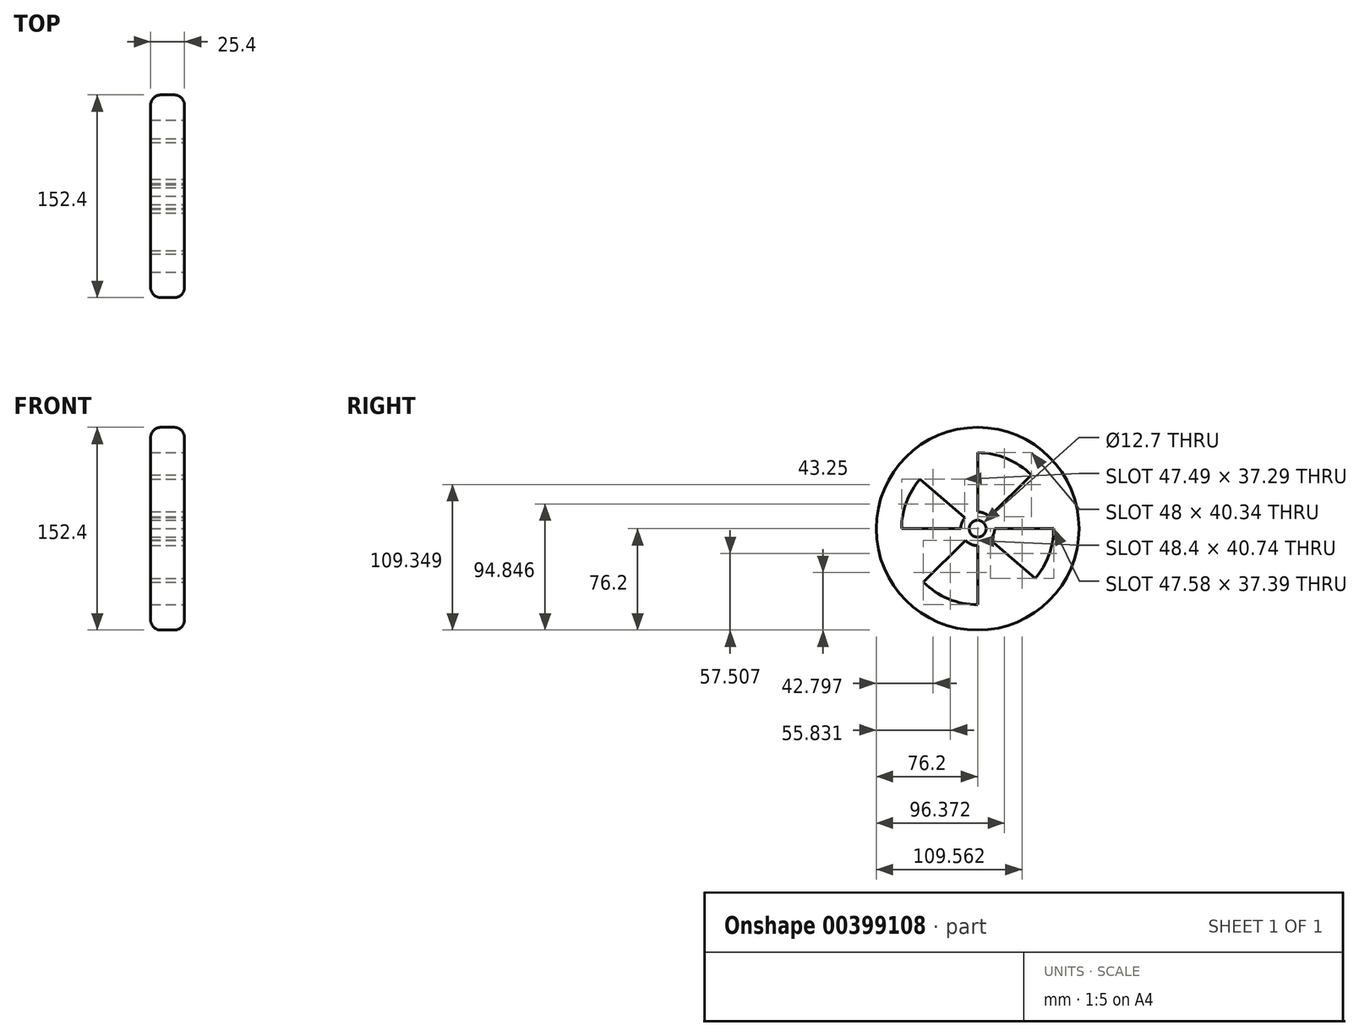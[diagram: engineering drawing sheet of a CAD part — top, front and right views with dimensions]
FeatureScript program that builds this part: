
annotation { "Feature Type Name" : "Feature", "Feature Type Description" : "" }
export const myFeature = defineFeature(function(context is Context, id is Id, definition is map)
    precondition{}
    {
        {
            var Q0;
            Q0=qCreatedBy(makeId("Right.planeOp"),FACE);
            var sketch = newSketch(context, id + "F0", { "sketchPlane" : qUnion([Q0])});
            skCircle(sketch, "E0", {"center": v(0, 0) * mm, "radius": 76.2 * mm});
            skSolve(sketch);
        }
        {
            var Q0;
            Q0=makeQuery(id+"F0.imprint","IMPRINT",FACE,{"disambiguationData":[TD([[makeQuery(id+"F0.imprint","IMPRINT",EDGE,{"derivedFrom":sQuery(id+"F0.wireOp",EDGE,"E0")}),1.0]])]});
            extrude(context, id + "F1", {"entities" : qUnion([Q0]), "depth" : 25.4 * mm});
        }
        {
            var Q0;
            Q0=makeQuery(id+"F1.opExtrude","CAP_FACE",FACE,{"disambiguationData":[OSD([sQuery(id+"F0.wireOp",EDGE,"E0")])],"isStart":false});
            var sketch = newSketch(context, id + "F2", { "sketchPlane" : qUnion([Q0])});
            skCircle(sketch, "E1", {"center": v(0, 0) * mm, "radius": 6.35 * mm});
            skSolve(sketch);
        }
        {
            var Q0;
            Q0=makeQuery(id+"F2.imprint","IMPRINT",FACE,{"disambiguationData":[TD([[makeQuery(id+"F2.imprint","IMPRINT",EDGE,{"derivedFrom":sQuery(id+"F2.wireOp",EDGE,"E1")}),1.0]])]});
            extrude(context, id + "F3", {"entities" : qUnion([Q0]), "operationType" : NewBodyOperationType.REMOVE, "oppositeDirection" : true, "depth" : 25.4 * mm});
        }
        {
            var Q0;
            Q0=makeQuery(id+"F1.opExtrude","CAP_FACE",FACE,{"disambiguationData":[OSD([sQuery(id+"F0.wireOp",EDGE,"E0")])],"isStart":false});
            var sketch = newSketch(context, id + "F4", { "sketchPlane" : qUnion([Q0])});
            skCircle(sketch, "E2", {"center": v(0, 0) * mm, "radius": 57.15 * mm});
            skLineSegment(sketch, "E3", {"start": v(0, 57.15) * mm, "end": v(0, -57.15) * mm});
            skLineSegment(sketch, "E4", {"start": v(-57.15, 0) * mm, "end": v(57.15, 0) * mm});
            skLineSegment(sketch, "E5", {"start": v(-43.3, 37.3) * mm, "end": v(43.22, -37.39) * mm});
            skLineSegment(sketch, "E6", {"start": v(40.34, 40.48) * mm, "end": v(-40.74, -40.08) * mm});
            skCircle(sketch, "E7", {"center": v(0, 0) * mm, "radius": 12.7 * mm});
            skSolve(sketch);
        }
        {
            var Q0;
            {var subQ0=sQuery(id+"F4.wireOp",EDGE,"E3");var subQ1=sQuery(id+"F4.wireOp",EDGE,"E2");var subQ2=makeQuery(id+"F4.imprint","INTERSECT",VERTEX,{"disambiguationData":[OD(1.0)],"derivedFrom":[subQ1,subQ0]});Q0=makeQuery(id+"F4.imprint","IMPRINT",FACE,{"disambiguationData":[TD([[makeQuery(id+"F4.imprint","IMPRINT",EDGE,{"disambiguationData":[TD([[subQ2,1.0]])],"derivedFrom":subQ1}),1.0]])]});}
            var Q1;
            {var subQ0=sQuery(id+"F4.wireOp",EDGE,"E4");var subQ1=sQuery(id+"F4.wireOp",EDGE,"E2");var subQ2=makeQuery(id+"F4.imprint","INTERSECT",VERTEX,{"disambiguationData":[OD(0.0)],"derivedFrom":[subQ1,subQ0]});Q1=makeQuery(id+"F4.imprint","IMPRINT",FACE,{"disambiguationData":[TD([[makeQuery(id+"F4.imprint","IMPRINT",EDGE,{"disambiguationData":[TD([[subQ2,1.0]])],"derivedFrom":subQ1}),1.0]])]});}
            var Q2;
            {var subQ0=sQuery(id+"F4.wireOp",EDGE,"E3");var subQ1=sQuery(id+"F4.wireOp",EDGE,"E2");var subQ2=makeQuery(id+"F4.imprint","INTERSECT",VERTEX,{"disambiguationData":[OD(0.0)],"derivedFrom":[subQ1,subQ0]});Q2=makeQuery(id+"F4.imprint","IMPRINT",FACE,{"disambiguationData":[TD([[makeQuery(id+"F4.imprint","IMPRINT",EDGE,{"disambiguationData":[TD([[subQ2,1.0]])],"derivedFrom":subQ1}),1.0]])]});}
            var Q3;
            {var subQ0=sQuery(id+"F4.wireOp",EDGE,"E4");var subQ1=sQuery(id+"F4.wireOp",EDGE,"E2");var subQ2=makeQuery(id+"F4.imprint","INTERSECT",VERTEX,{"disambiguationData":[OD(1.0)],"derivedFrom":[subQ1,subQ0]});Q3=makeQuery(id+"F4.imprint","IMPRINT",FACE,{"disambiguationData":[TD([[makeQuery(id+"F4.imprint","IMPRINT",EDGE,{"disambiguationData":[TD([[subQ2,1.0]])],"derivedFrom":subQ1}),1.0]])]});}
            extrude(context, id + "F5", {"entities" : qUnion([Q0, Q1, Q2, Q3]), "operationType" : NewBodyOperationType.REMOVE, "oppositeDirection" : true, "depth" : 25.4 * mm});
        }
        {
            var Q0;
            Q0=makeQuery(id+"F1.opExtrude","CAP_EDGE",EDGE,{"disambiguationData":[OSD([sQuery(id+"F0.wireOp",EDGE,"E0")])],"isStart":false});
            var Q1;
            Q1=makeQuery(id+"F1.opExtrude","CAP_EDGE",EDGE,{"disambiguationData":[OSD([sQuery(id+"F0.wireOp",EDGE,"E0")])],"isStart":true});
            fillet(context, id + "F6", {"entities" : qUnion([Q0, Q1]), "radius" : 7.62 * mm, "tangentPropagation" : true, "allowEdgeOverflow" : false});
        }
    });
